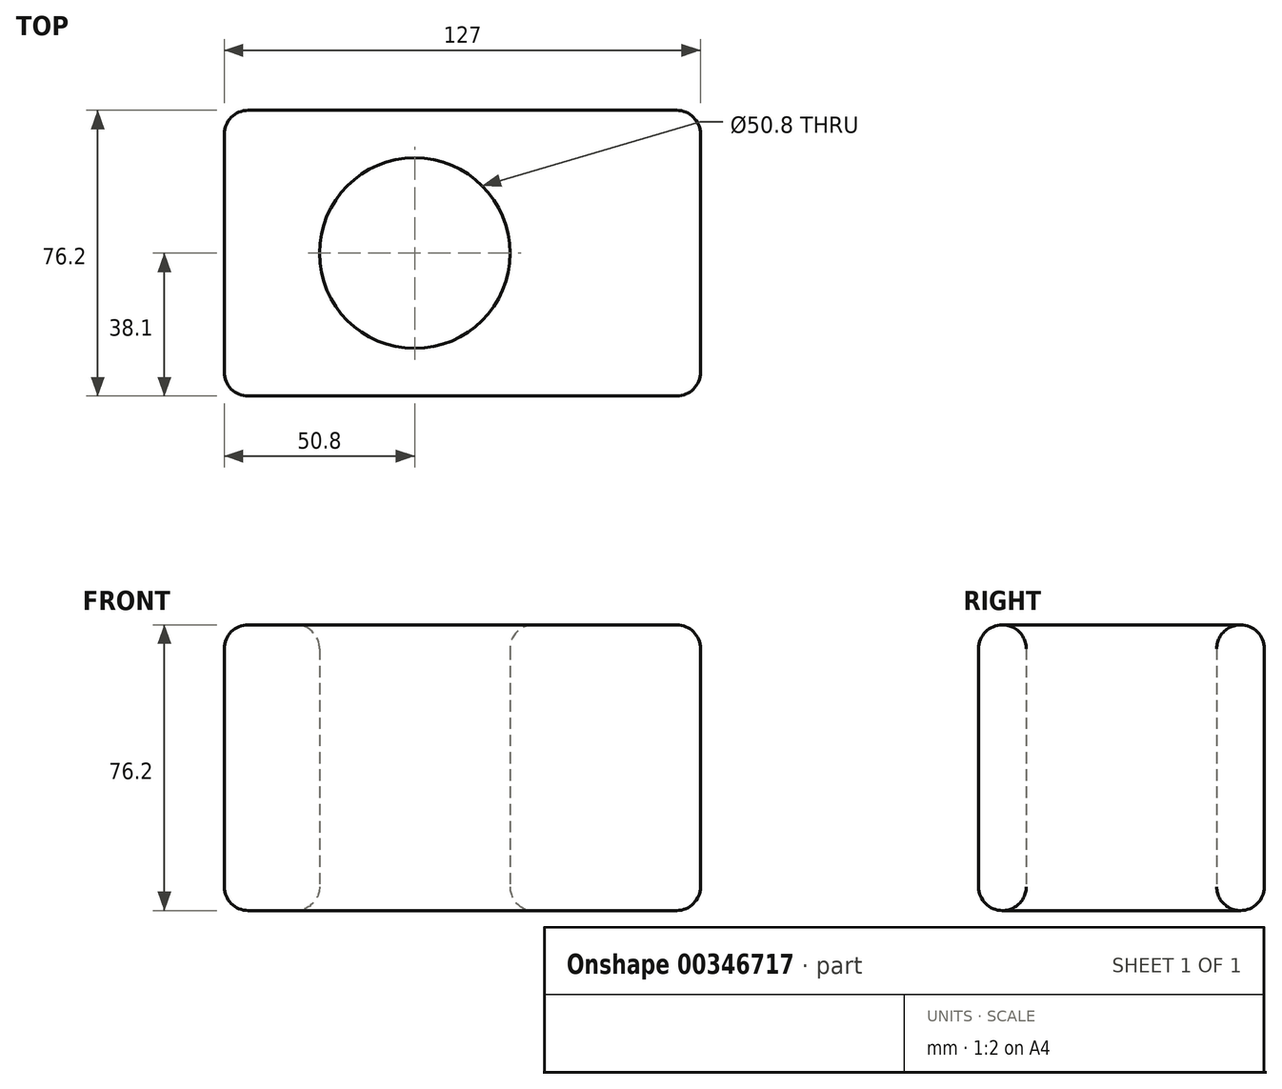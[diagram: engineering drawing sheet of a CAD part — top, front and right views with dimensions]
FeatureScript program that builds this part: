
annotation { "Feature Type Name" : "Feature", "Feature Type Description" : "" }
export const myFeature = defineFeature(function(context is Context, id is Id, definition is map)
    precondition{}
    {
        {
            var Q0;
            Q0=qCreatedBy(makeId("Top.planeOp"),FACE);
            var sketch = newSketch(context, id + "F0", { "sketchPlane" : qUnion([Q0])});
            skLineSegment(sketch, "E0.bottom", {"start": v(-50.8, 38.1) * mm, "end": v(50.8, 38.1) * mm});
            skLineSegment(sketch, "E0.top", {"start": v(-50.8, -38.1) * mm, "end": v(50.8, -38.1) * mm});
            skLineSegment(sketch, "E0.left", {"start": v(-50.8, 38.1) * mm, "end": v(-50.8, -38.1) * mm});
            skLineSegment(sketch, "E0.right", {"start": v(50.8, 38.1) * mm, "end": v(50.8, -38.1) * mm});
            skPoint(sketch, "E0.middle", {"position": v(0, 0) * mm});
            skCircle(sketch, "E1", {"center": v(0, 0) * mm, "radius": 25.4 * mm});
            skSolve(sketch);
        }
        {
            var Q0;
            Q0=makeQuery(id+"F0.imprint","IMPRINT",FACE,{"disambiguationData":[TD([[makeQuery(id+"F0.imprint","IMPRINT",EDGE,{"derivedFrom":sQuery(id+"F0.wireOp",EDGE,"E0.bottom")}),-1.0]])]});
            extrude(context, id + "F1", {"entities" : qUnion([Q0]), "endBound" : BoundingType.SYMMETRIC, "depth" : 76.2 * mm});
        }
        {
            var Q0;
            Q0=makeQuery(id+"F1.opExtrude","SWEPT_FACE",FACE,{"disambiguationData":[OSD([sQuery(id+"F0.wireOp",EDGE,"E0.right")])]});
            extrude(context, id + "F2", {"entities" : qUnion([Q0]), "operationType" : NewBodyOperationType.ADD, "depth" : 25.4 * mm});
        }
        {
            var Q0;
            Q0=makeQuery(id+"F1.opExtrude","CAP_FACE",FACE,{"disambiguationData":[OSD([sQuery(id+"F0.wireOp",EDGE,"E0.bottom"),sQuery(id+"F0.wireOp",EDGE,"E0.top"),sQuery(id+"F0.wireOp",EDGE,"E0.left"),sQuery(id+"F0.wireOp",EDGE,"E0.right"),sQuery(id+"F0.wireOp",EDGE,"E1")])],"isStart":false});
            var Q1;
            Q1=makeQuery(id+"F1.opExtrude","SWEPT_FACE",FACE,{"disambiguationData":[OSD([sQuery(id+"F0.wireOp",EDGE,"E0.left")])]});
            var Q2;
            Q2=makeQuery(id+"F1.opExtrude","SWEPT_FACE",FACE,{"disambiguationData":[OSD([sQuery(id+"F0.wireOp",EDGE,"E0.bottom")])]});
            var Q3;
            Q3=makeQuery(id+"F1.opExtrude","SWEPT_FACE",FACE,{"disambiguationData":[OSD([sQuery(id+"F0.wireOp",EDGE,"E0.right")])]});
            var Q4;
            Q4=makeQuery(id+"F1.opExtrude","SWEPT_FACE",FACE,{"disambiguationData":[OSD([sQuery(id+"F0.wireOp",EDGE,"E0.top")])]});
            var Q5;
            Q5=makeQuery(id+"F1.opExtrude","CAP_FACE",FACE,{"disambiguationData":[OSD([sQuery(id+"F0.wireOp",EDGE,"E0.bottom"),sQuery(id+"F0.wireOp",EDGE,"E0.top"),sQuery(id+"F0.wireOp",EDGE,"E0.left"),sQuery(id+"F0.wireOp",EDGE,"E0.right"),sQuery(id+"F0.wireOp",EDGE,"E1")])],"isStart":true});
            fillet(context, id + "F3", {"entities" : qUnion([Q0, Q1, Q2, Q3, Q4, Q5]), "radius" : 6.35 * mm, "tangentPropagation" : true, "allowEdgeOverflow" : false});
        }
    });
